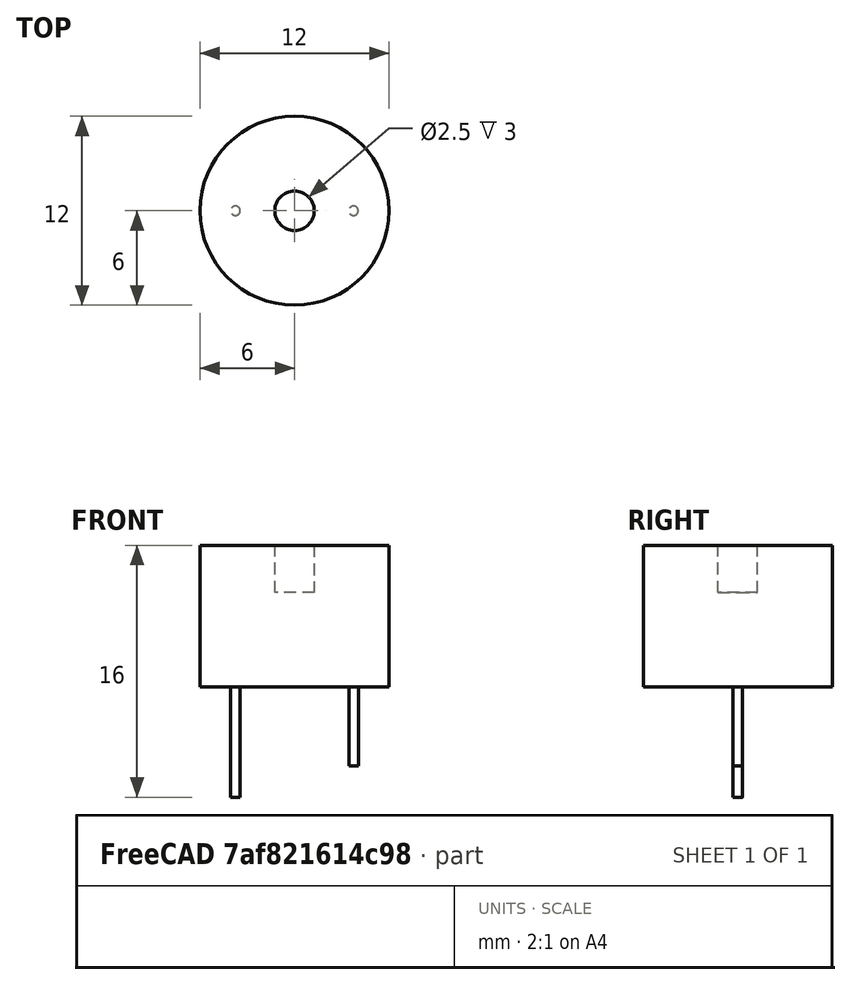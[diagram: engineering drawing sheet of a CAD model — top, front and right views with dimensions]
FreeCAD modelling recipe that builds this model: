
FCSTD DOCUMENT  (FreeCAD 0.14R3692 (Git))
Label: Buzzer
License: CC-BY 3.0
LicenseURL: http://creativecommons.org/licenses/by/3.0/
objects: Part::Cylinder×3, Sketcher::SketchObject×1, PartDesign::Pocket×1, Part::MultiFuse×1
note: 7 computed .brp shape members not serialized (recipe doc carries the construction recipe); baked Part::Feature solids carry a one-line shape summary decoded from their .brp

FEATURE [Part::Cylinder] Cylinder  label="BodyCylinder"
  Angle = 360
  Height = 9
  Radius = 6
FEATURE [Sketcher::SketchObject] Sketch  label="HoleSketch"
  Placement = pos=(0,0,9) rot=(0,0,1;0rad)
  Support = -> Cylinder [Face2]
  sketch-geometry (1):
    g0: Circle CenterX=0 CenterY=0 CenterZ=0 NormalX=0 NormalY=0 NormalZ=1 Radius=1.25
  constraints (2):
    c: Coincident(g0,g-1)
    c: Radius(g0) = 1.25
FEATURE [PartDesign::Pocket] Pocket  label="HolePocket"
  Length = 3
  Sketch = -> Sketch
  Type = 0
FEATURE [Part::Cylinder] Cylinder001  label="AnodeCylinder001"
  Angle = 360
  Height = 7
  Placement = pos=(-3.75,0,-7) rot=(0,0,1;0rad)
  Radius = 0.3
FEATURE [Part::Cylinder] Cylinder002  label="CathodeCylinder002"
  Angle = 360
  Height = 5
  Placement = pos=(3.75,0,-5) rot=(0,0,1;0rad)
  Radius = 0.3
FEATURE [Part::MultiFuse] Fusion  label="BuzzerFusion"
  Shapes = -> [Cylinder001,Pocket,Cylinder002]
